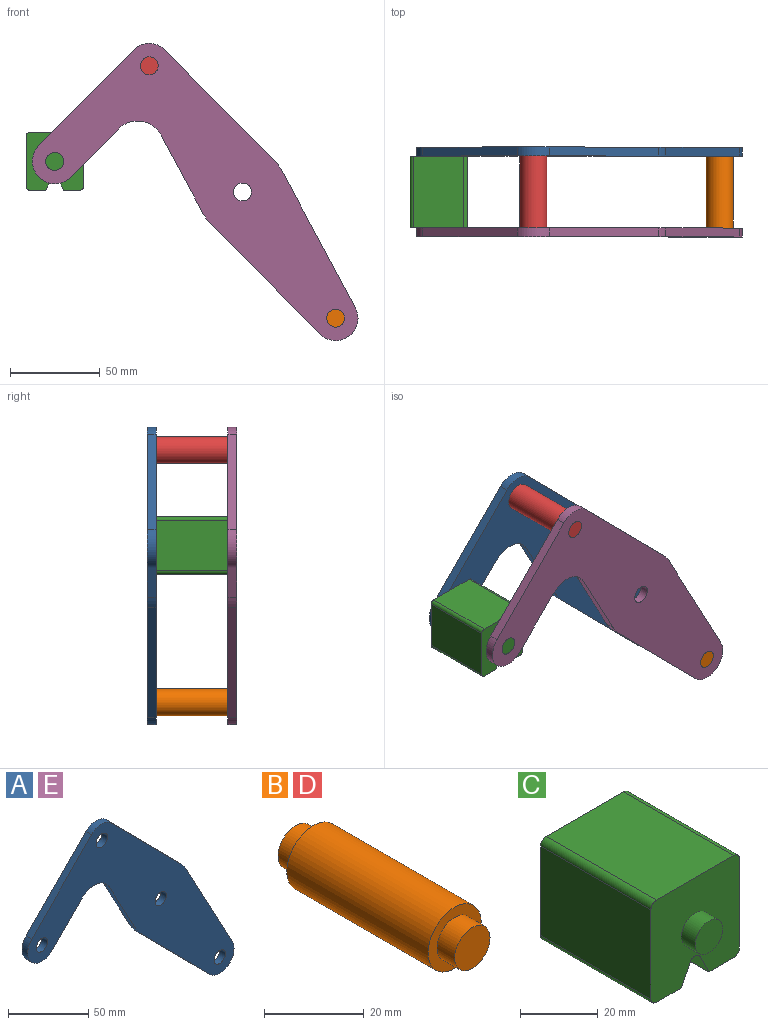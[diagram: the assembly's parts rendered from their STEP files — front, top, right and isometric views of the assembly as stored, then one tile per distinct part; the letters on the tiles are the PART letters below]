
ASSEMBLY  parts=5 mates=3
PART A: 18 faces, bbox 181.7x5x165.8 mm
  f0: plane 43.49x23.35mm, normal (-0.88,0,-0.47), area 246.8mm2, adj f1,f14,f16,f17
  f1: cylinder r=25mm len=5.75mm, axis (0,1,0), area 35.8mm2, adj f0,f2,f16,f17
  f2: plane 61.6x60.87mm, normal (-0.71,0,-0.7), area 433mm2, adj f1,f3,f16,f17
  f3: cylinder r=12.5mm len=21.39mm, axis (0,1,0), area 178.4mm2, adj f2,f4,f16,f17
  f4: plane 76.3x40.96mm, normal (0.88,0,0.47), area 433mm2, adj f3,f5,f16,f17
  f5: cylinder r=25mm len=5.75mm, axis (0,1,0), area 35.8mm2, adj f4,f6,f16,f17
  f6: plane 61.6x60.87mm, normal (0.71,0,0.7), area 433mm2, adj f5,f7,f16,f17
  f7: cylinder r=12.5mm len=17.78mm, axis (0,1,0), area 98.9mm2, adj f6,f8,f16,f17
  f8: plane 53.35x52.71mm, normal (-0.71,0,0.7), area 375mm2, adj f7,f9,f16,f17
  f9: cylinder r=12.5mm len=21.39mm, axis (0,1,0), area 196.3mm2, adj f8,f10,f16,f17
  f10: plane 26.86x26.54mm, normal (0.71,0,-0.7), area 188.8mm2, adj f9,f14,f16,f17
  f11: cylinder r=5mm len=10mm, axis (0,1,0), area 157.1mm2, adj f16,f17
  f12: cylinder r=5mm len=10mm, axis (0,1,0), area 157.1mm2, adj f16,f17
  f13: cylinder r=5mm len=10mm, axis (0,1,0), area 157.1mm2, adj f16,f17
  f14: cylinder r=15mm len=23.89mm, axis (0,1,0), area 140.2mm2, adj f0,f10,f16,f17
  f15: cylinder r=5mm len=10mm, axis (0,1,0), area 157.1mm2, adj f16,f17
  f16: plane 181.66x165.78mm, normal (0,-1,0), area 8710.1mm2, adj f0,f1,f2,f3,f4,f5,f6,f7
  f17: plane 181.66x165.78mm, normal (0,1,0), area 8710.1mm2, adj f0,f1,f2,f3,f4,f5,f6,f7
PART B: 7 faces, bbox 15x50x15 mm
  f0: cylinder r=7.5mm len=40mm, axis (0,-1,0), area 1885mm2, adj f2,f5
  f1: cylinder r=5mm len=10mm, axis (0,1,0), area 157.1mm2, adj f2,f3
  f2: plane 15x15mm, normal (0,-1,0), area 98.2mm2, adj f0,f1
  f3: plane 10x10mm, normal (0,-1,0), area 78.5mm2, adj f1
  f4: cylinder r=5mm len=10mm, axis (0,-1,0), area 157.1mm2, adj f5,f6
  f5: plane 15x15mm, normal (0,1,0), area 98.2mm2, adj f0,f4
  f6: plane 10x10mm, normal (0,1,0), area 78.5mm2, adj f4
PART C: 18 faces, bbox 32.1x50x32.1 mm
  f0: plane 40x28.08mm, normal (1,0,0), area 1123.1mm2, adj f4,f10,f13,f14
  f1: plane 40x9.04mm, normal (0,0,-1), area 361.6mm2, adj f2,f4,f10,f14
  f2: plane 40x6.42mm, normal (-0.89,0,-0.45), area 287.2mm2, adj f1,f4,f10,f15
  f3: plane 40x6.42mm, normal (0.89,0,-0.45), area 287.2mm2, adj f4,f5,f10,f15
  f4: plane 32.08x32.08mm, normal (0,-1,0), area 900.6mm2, adj f0,f1,f2,f3,f5,f6,f7,f9
  f5: plane 40x9.04mm, normal (0,0,-1), area 361.6mm2, adj f3,f4,f10,f16
  f6: plane 40x28.08mm, normal (0,0,1), area 1123.1mm2, adj f4,f10,f13,f17
  f7: plane 40x28.08mm, normal (-1,0,0), area 1123.1mm2, adj f4,f10,f16,f17
  f8: plane 10x10mm, normal (0,-1,0), area 78.5mm2, adj f9
  f9: cylinder r=5mm len=10mm, axis (0,1,0), area 157.1mm2, adj f4,f8
  f10: plane 32.08x32.08mm, normal (0,1,0), area 900.6mm2, adj f0,f1,f2,f3,f5,f6,f7,f12
  f11: plane 10x10mm, normal (0,1,0), area 78.5mm2, adj f12
  f12: cylinder r=5mm len=10mm, axis (0,-1,0), area 157.1mm2, adj f10,f11
  f13: cylinder r=2mm len=40mm, axis (0,1,0), area 125.7mm2, adj f0,f4,f6,f10
  f14: cylinder r=2mm len=40mm, axis (0,-1,0), area 125.7mm2, adj f0,f1,f4,f10
  f15: cylinder r=2mm len=40mm, axis (0,1,0), area 177.1mm2, adj f2,f3,f4,f10
  f16: cylinder r=2mm len=40mm, axis (0,1,0), area 125.7mm2, adj f4,f5,f7,f10
  f17: cylinder r=2mm len=40mm, axis (0,-1,0), area 125.7mm2, adj f4,f6,f7,f10
PART D: same geometry as B
PART E: same geometry as A
PLACE A t=(-5.01,22.13,-5.65)mm
PLACE B t=(98.94,-22.87,-146.43)mm
PLACE C t=(-5.01,-22.87,-5.65)mm
PLACE D t=(-5.01,-22.87,-5.65)mm
PLACE E t=(-5.01,-22.87,-5.65)mm fixed
MATE revolute C.f9 <-> E.f9  axis (0,-1,0) through (-109.7,-22.87,11.39)mm
MATE fastened B.f0 <-> A.f3  axis (0,1,0) through (46.97,17.13,-76.04)mm
MATE fastened A.f7 <-> D.f0  axis (0,-1,0) through (-56.99,17.13,64.74)mm
